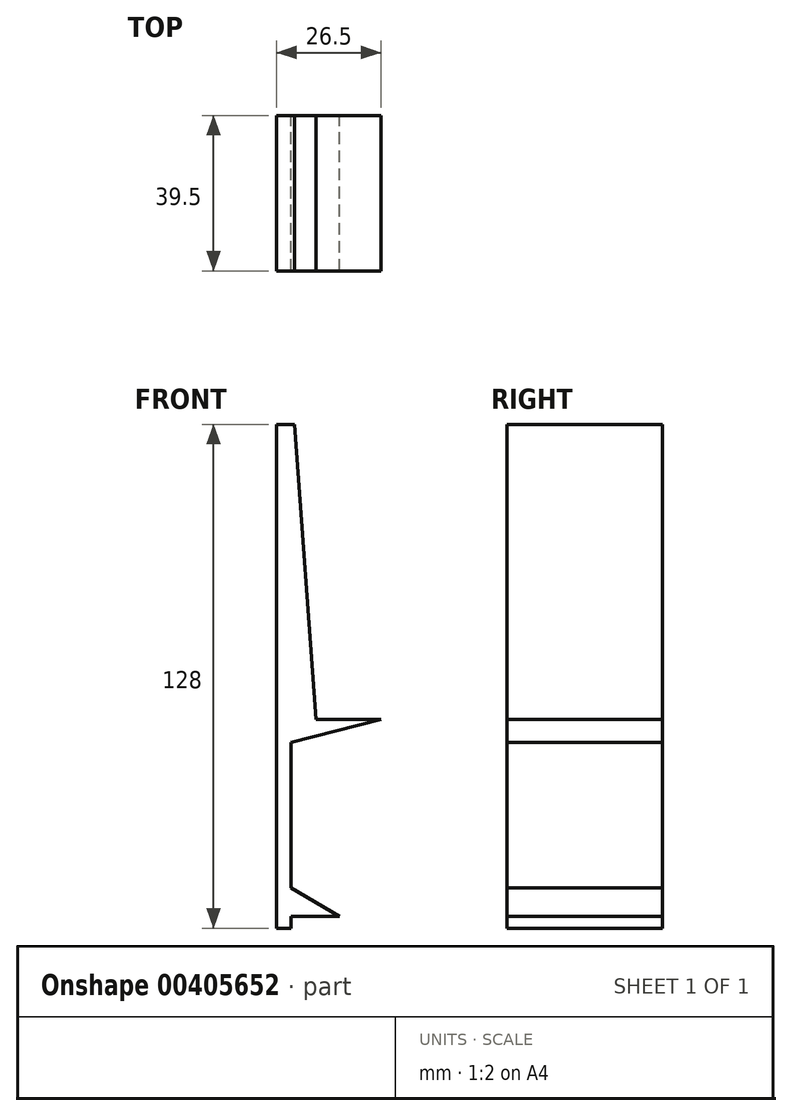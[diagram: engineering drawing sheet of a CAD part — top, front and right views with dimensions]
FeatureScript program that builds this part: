
annotation { "Feature Type Name" : "Feature", "Feature Type Description" : "" }
export const myFeature = defineFeature(function(context is Context, id is Id, definition is map)
    precondition{}
    {
        {
            var Q0;
            Q0=qCreatedBy(makeId("Front.planeOp"),FACE);
            var sketch = newSketch(context, id + "F0", { "sketchPlane" : qUnion([Q0])});
            skLineSegment(sketch, "E0.bottom", {"start": v(0, 0) * mm, "end": v(3.6, 0) * mm});
            skLineSegment(sketch, "E0.top", {"start": v(0, -53) * mm, "end": v(3.6, -53) * mm});
            skLineSegment(sketch, "E0.left", {"start": v(0, 0) * mm, "end": v(0, -53) * mm});
            skLineSegment(sketch, "E0.right", {"start": v(3.6, 0) * mm, "end": v(3.6, -53) * mm});
            skLineSegment(sketch, "E1", {"start": v(3.6, -50) * mm, "end": v(15.97, -50) * mm});
            skLineSegment(sketch, "E2", {"start": v(15.97, -50) * mm, "end": v(3.6, -42.76) * mm});
            skLineSegment(sketch, "E3", {"start": v(3.6, 0) * mm, "end": v(26.5, 0) * mm});
            skLineSegment(sketch, "E4", {"start": v(26.5, 0) * mm, "end": v(3.6, -5.75) * mm});
            skLineSegment(sketch, "E5", {"start": v(0, 0) * mm, "end": v(0, 75) * mm});
            skLineSegment(sketch, "E6", {"start": v(0, 75) * mm, "end": v(4.6, 75) * mm});
            skLineSegment(sketch, "E7", {"start": v(4.6, 75) * mm, "end": v(10.07, 0) * mm});
            skSolve(sketch);
        }
        {
            var Q0;
            Q0 = qSketchRegion(id + "F0", true);
            extrude(context, id + "F1", {"entities" : qUnion([Q0]), "depth" : 39.5 * mm});
        }
    });
